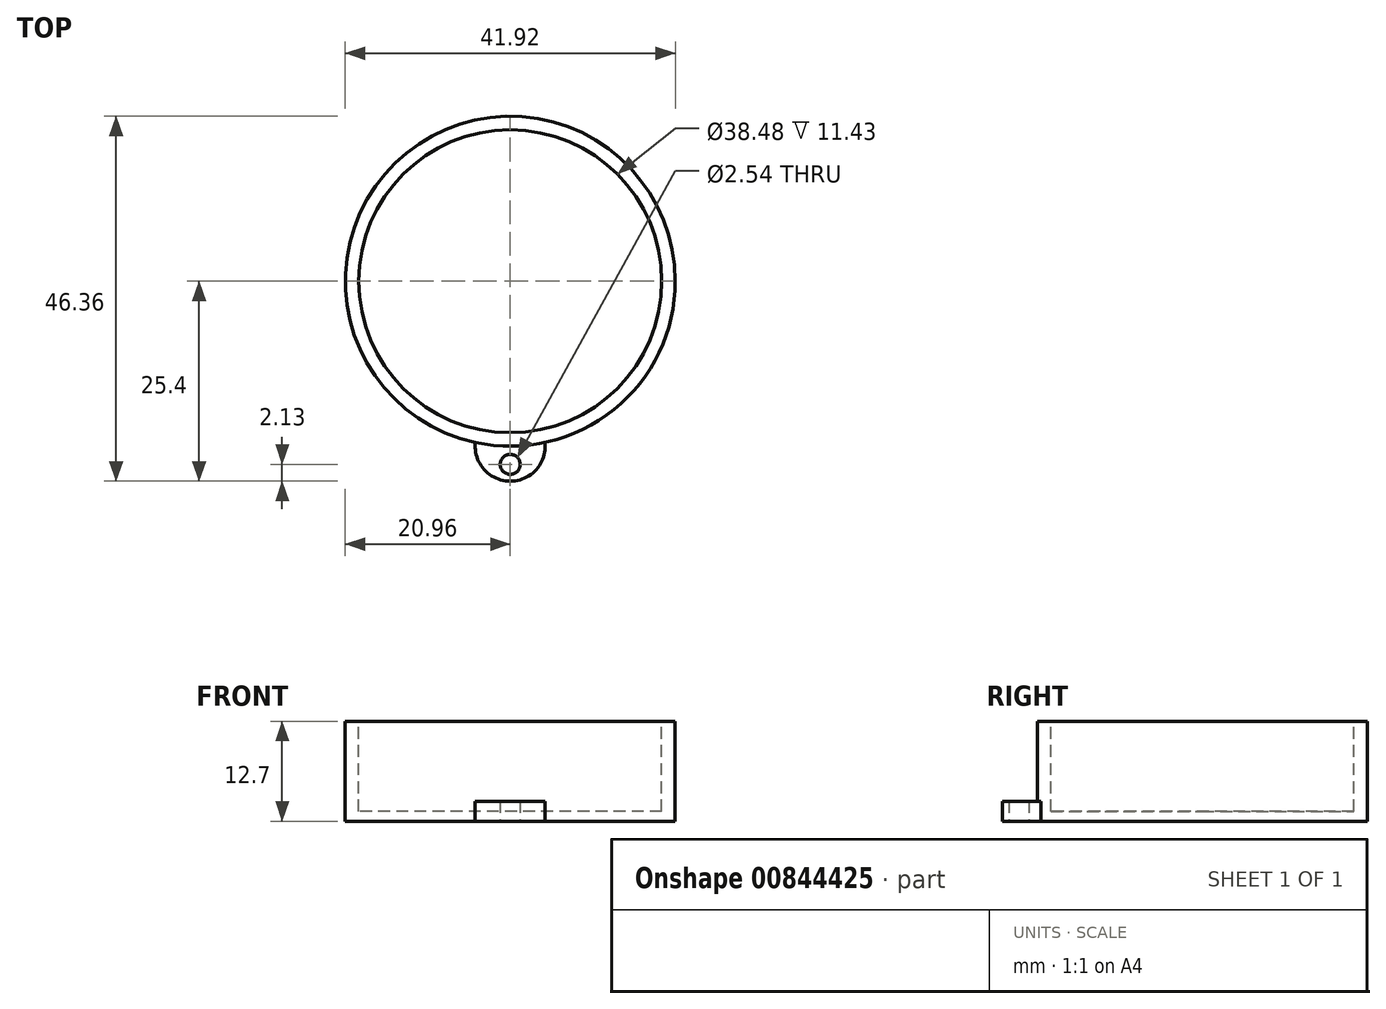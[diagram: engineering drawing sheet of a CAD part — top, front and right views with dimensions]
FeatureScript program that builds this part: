
annotation { "Feature Type Name" : "Feature", "Feature Type Description" : "" }
export const myFeature = defineFeature(function(context is Context, id is Id, definition is map)
    precondition{}
    {
        {
            var Q0;
            Q0=qCreatedBy(makeId("Top.planeOp"),FACE);
            var sketch = newSketch(context, id + "F0", { "sketchPlane" : qUnion([Q0])});
            skCircle(sketch, "E0", {"center": v(0, 0) * mm, "radius": 20.96 * mm});
            skSolve(sketch);
        }
        {
            var Q0;
            Q0=makeQuery(id+"F0.imprint","IMPRINT",FACE,{"disambiguationData":[TD([[makeQuery(id+"F0.imprint","IMPRINT",EDGE,{"derivedFrom":sQuery(id+"F0.wireOp",EDGE,"E0")}),1.0]])]});
            extrude(context, id + "F1", {"entities" : qUnion([Q0]), "depth" : 12.7 * mm, "offsetDistance" : 25.4 * mm});
        }
        {
            var Q0;
            Q0=makeQuery(id+"F1.opExtrude","CAP_FACE",FACE,{"disambiguationData":[OSD([sQuery(id+"F0.wireOp",EDGE,"E0")])],"isStart":false});
            var sketch = newSketch(context, id + "F2", { "sketchPlane" : qUnion([Q0])});
            skCircle(sketch, "E1", {"center": v(0, 0) * mm, "radius": 19.24 * mm});
            skSolve(sketch);
        }
        {
            var Q0;
            Q0=makeQuery(id+"F2.imprint","IMPRINT",FACE,{"disambiguationData":[TD([[makeQuery(id+"F2.imprint","IMPRINT",EDGE,{"derivedFrom":sQuery(id+"F2.wireOp",EDGE,"E1")}),1.0]])]});
            extrude(context, id + "F3", {"entities" : qUnion([Q0]), "operationType" : NewBodyOperationType.REMOVE, "oppositeDirection" : true, "depth" : 11.43 * mm, "offsetDistance" : 25.4 * mm});
        }
        {
            var Q0;
            Q0=makeQuery(id+"F1.opExtrude","CAP_FACE",FACE,{"disambiguationData":[OSD([sQuery(id+"F0.wireOp",EDGE,"E0")])],"isStart":true});
            var sketch = newSketch(context, id + "F4", { "sketchPlane" : qUnion([Q0])});
            skCircle(sketch, "E2", {"center": v(0, 23.27) * mm, "radius": 1.27 * mm});
            skCircle(sketch, "E3", {"center": v(0, 20.96) * mm, "radius": 4.45 * mm});
            skSolve(sketch);
        }
        {
            var Q0;
            Q0=makeQuery(id+"F4.imprint","IMPRINT",FACE,{"disambiguationData":[TD([[makeQuery(id+"F4.imprint","IMPRINT",EDGE,{"derivedFrom":sQuery(id+"F4.wireOp",EDGE,"E2")}),-1.0]])]});
            extrude(context, id + "F5", {"entities" : qUnion([Q0]), "operationType" : NewBodyOperationType.ADD, "oppositeDirection" : true, "depth" : 2.54 * mm, "offsetDistance" : 25.4 * mm});
        }
    });
